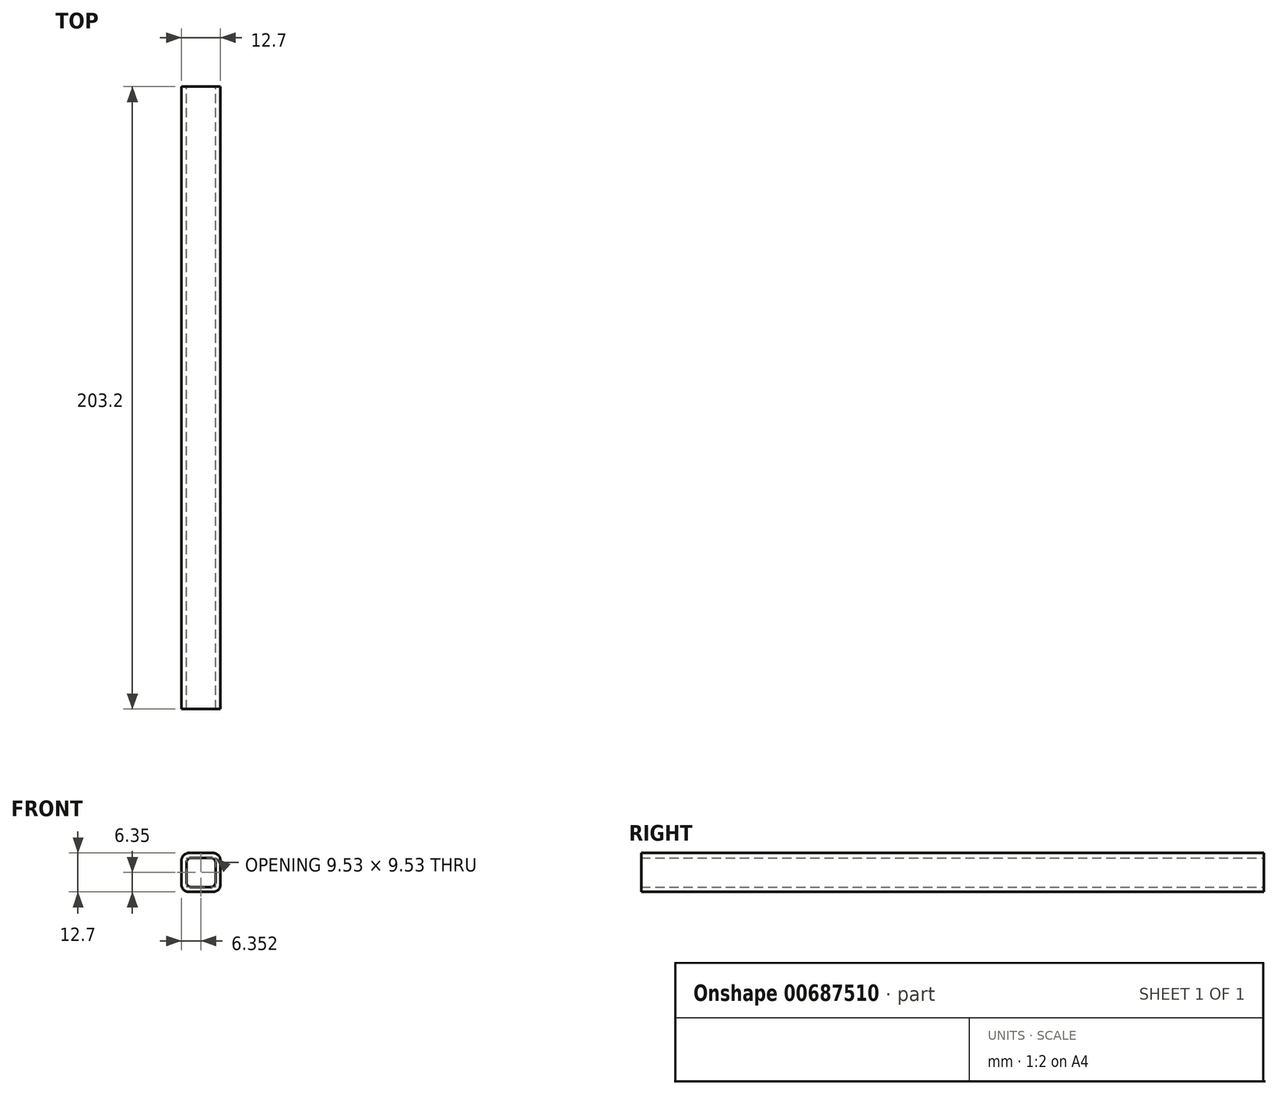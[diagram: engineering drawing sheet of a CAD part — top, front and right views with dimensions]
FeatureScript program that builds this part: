
annotation { "Feature Type Name" : "Feature", "Feature Type Description" : "" }
export const myFeature = defineFeature(function(context is Context, id is Id, definition is map)
    precondition{}
    {
        {
            var Q0;
            Q0=qCreatedBy(makeId("Front.planeOp"),FACE);
            var sketch = newSketch(context, id + "F0", { "sketchPlane" : qUnion([Q0])});
            skLineSegment(sketch, "E0.bottom", {"start": v(7.7, 0) * mm, "end": v(-0.25, 0) * mm});
            skLineSegment(sketch, "E0.top", {"start": v(7.7, -12.7) * mm, "end": v(-0.25, -12.7) * mm});
            skLineSegment(sketch, "E0.left", {"start": v(10.07, -2.38) * mm, "end": v(10.07, -10.32) * mm});
            skLineSegment(sketch, "E0.right", {"start": v(-2.63, -2.38) * mm, "end": v(-2.63, -10.32) * mm});
            skPoint(sketch, "E0.middle", {"position": v(3.72, -6.35) * mm});
            skPoint(sketch, "E1.visualSharp", {"position": v(-2.63, 0) * mm});
            skArc(sketch, "E1.filletArc", {"start": v(-0.25, 0) * mm, "mid": v(-1.93, -0.7) * mm, "end": v(-2.63, -2.38) * mm});
            skPoint(sketch, "E2.visualSharp", {"position": v(-2.63, -12.7) * mm});
            skArc(sketch, "E2.filletArc", {"start": v(-2.63, -10.32) * mm, "mid": v(-1.93, -12) * mm, "end": v(-0.25, -12.7) * mm});
            skPoint(sketch, "E3.visualSharp", {"position": v(10.07, -12.7) * mm});
            skArc(sketch, "E3.filletArc", {"start": v(7.7, -12.7) * mm, "mid": v(9.37, -12) * mm, "end": v(10.07, -10.32) * mm});
            skPoint(sketch, "E4.visualSharp", {"position": v(10.07, 0) * mm});
            skArc(sketch, "E4.filletArc", {"start": v(10.07, -2.38) * mm, "mid": v(9.37, -0.7) * mm, "end": v(7.7, 0) * mm});
            skLineSegment(sketch, "E5.bottom", {"start": v(6.9, -1.59) * mm, "end": v(0.55, -1.59) * mm});
            skLineSegment(sketch, "E5.top", {"start": v(6.9, -11.11) * mm, "end": v(0.55, -11.11) * mm});
            skLineSegment(sketch, "E5.left", {"start": v(8.48, -3.17) * mm, "end": v(8.48, -9.53) * mm});
            skLineSegment(sketch, "E5.right", {"start": v(-1.04, -3.18) * mm, "end": v(-1.04, -9.53) * mm});
            skPoint(sketch, "E6.visualSharp", {"position": v(-1.04, -1.59) * mm});
            skArc(sketch, "E6.filletArc", {"start": v(0.55, -1.59) * mm, "mid": v(-0.58, -2.05) * mm, "end": v(-1.04, -3.18) * mm});
            skPoint(sketch, "E7.visualSharp", {"position": v(8.48, -1.59) * mm});
            skArc(sketch, "E7.filletArc", {"start": v(8.48, -3.17) * mm, "mid": v(8.02, -2.05) * mm, "end": v(6.9, -1.59) * mm});
            skPoint(sketch, "E8.visualSharp", {"position": v(8.48, -11.11) * mm});
            skArc(sketch, "E8.filletArc", {"start": v(6.9, -11.11) * mm, "mid": v(8.02, -10.65) * mm, "end": v(8.48, -9.53) * mm});
            skPoint(sketch, "E9.visualSharp", {"position": v(-1.04, -11.11) * mm});
            skArc(sketch, "E9.filletArc", {"start": v(-1.04, -9.53) * mm, "mid": v(-0.58, -10.65) * mm, "end": v(0.55, -11.11) * mm});
            skSolve(sketch);
        }
        {
            var Q0;
            Q0=qSketchRegion(id+"F0",true);
            extrude(context, id + "F1", {"entities" : qUnion([Q0]), "depth" : 203.2 * mm, "offsetDistance" : 25.4 * mm});
        }
    });
